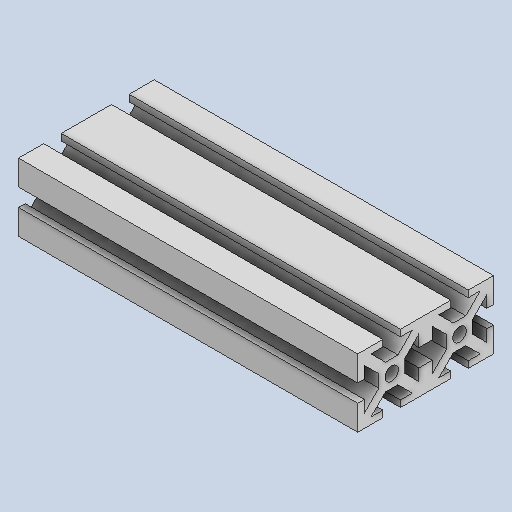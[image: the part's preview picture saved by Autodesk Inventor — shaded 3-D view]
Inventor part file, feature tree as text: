
AUTODESK INVENTOR PART (.ipt)
format: ipt  version: 2023 (Build 270158030, 158C)  size: 204,800 bytes
history: native  units: in
note: dims shown in document units (in); Inventor stores cm internally (conversion verified against a paired STEP export)
features: extrude x1, sketch x1
ambient origin geometry x8: Origin, YZ Plane, XZ Plane, XY Plane, X Axis, Y Axis, Z Axis, Center Point
bodies: Solid1 (feature_tree)
feature tree (2):
  extrude  "Extrusion1"  Depth=0.0975in
  sketch  "Sketch1"  dims[d2=0.37in d3=0.0975in d7=0.0975in d10=0.0975in d11=1.0in d13=0.0975in d16=0.0975in d17=0.37in d23=0.0975in d25=1.0in d32=0.175in d33=0.175in d35=135.0deg d36=0.175in d37=0.175in d38=0.0975in d40=0.175in d41=0.175in d42=0.175in d43=0.175in d44=0.2in d45=5.0in d46=0.0in]
